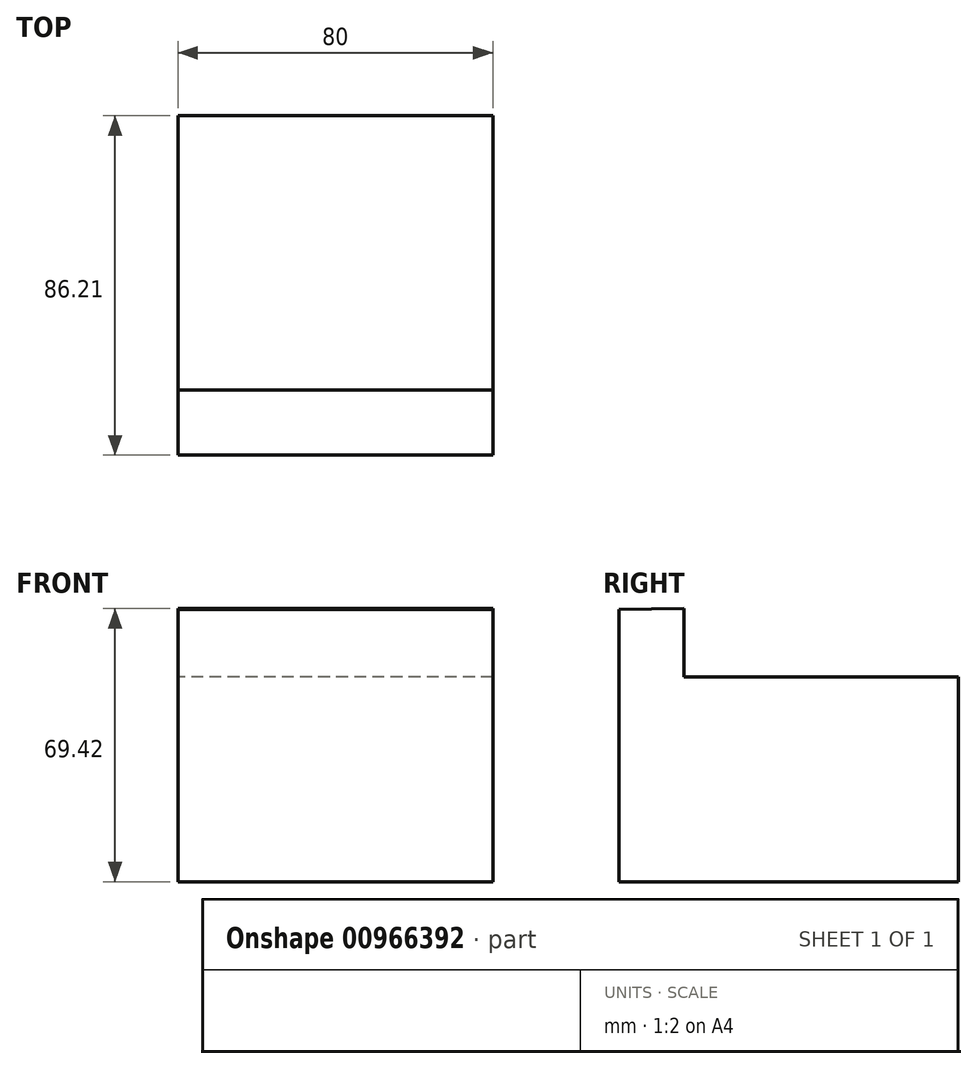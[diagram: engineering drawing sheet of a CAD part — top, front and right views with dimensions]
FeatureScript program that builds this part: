
annotation { "Feature Type Name" : "Feature", "Feature Type Description" : "" }
export const myFeature = defineFeature(function(context is Context, id is Id, definition is map)
    precondition{}
    {
        {
            var Q0;
            Q0=qCreatedBy(makeId("Right.planeOp"),FACE);
            var sketch = newSketch(context, id + "F0", { "sketchPlane" : qUnion([Q0])});
            skLineSegment(sketch, "E0.bottom", {"start": v(63.5, -50.8) * mm, "end": v(-63.5, -50.8) * mm, "construction": true});
            skLineSegment(sketch, "E0.top", {"start": v(63.5, 50.8) * mm, "end": v(-63.5, 50.8) * mm, "construction": true});
            skLineSegment(sketch, "E0.left", {"start": v(63.5, -50.8) * mm, "end": v(63.5, 50.8) * mm, "construction": true});
            skLineSegment(sketch, "E0.right", {"start": v(-63.5, -50.8) * mm, "end": v(-63.5, 50.8) * mm, "construction": true});
            skPoint(sketch, "E0.middle", {"position": v(0, 0) * mm});
            skLineSegment(sketch, "E1", {"start": v(-49.91, 38.9) * mm, "end": v(-49.91, -30.24) * mm});
            skLineSegment(sketch, "E2", {"start": v(-49.91, -30.24) * mm, "end": v(36.3, -30.24) * mm});
            skLineSegment(sketch, "E3", {"start": v(36.3, -30.24) * mm, "end": v(36.3, 21.83) * mm});
            skLineSegment(sketch, "E4", {"start": v(36.3, 21.83) * mm, "end": v(-33.42, 21.83) * mm});
            skLineSegment(sketch, "E5", {"start": v(-33.42, 21.83) * mm, "end": v(-33.42, 39.18) * mm});
            skLineSegment(sketch, "E6", {"start": v(-33.42, 39.18) * mm, "end": v(-49.91, 38.9) * mm});
            skSolve(sketch);
        }
        {
            var Q0;
            Q0=makeQuery(id+"F0.imprint","IMPRINT",FACE,{"disambiguationData":[TD([[makeQuery(id+"F0.imprint","IMPRINT",EDGE,{"derivedFrom":sQuery(id+"F0.wireOp",EDGE,"E1")}),1.0]])]});
            extrude(context, id + "F1", {"entities" : qUnion([Q0]), "depth" : 80 * mm, "offsetDistance" : 25 * mm});
        }
    });
